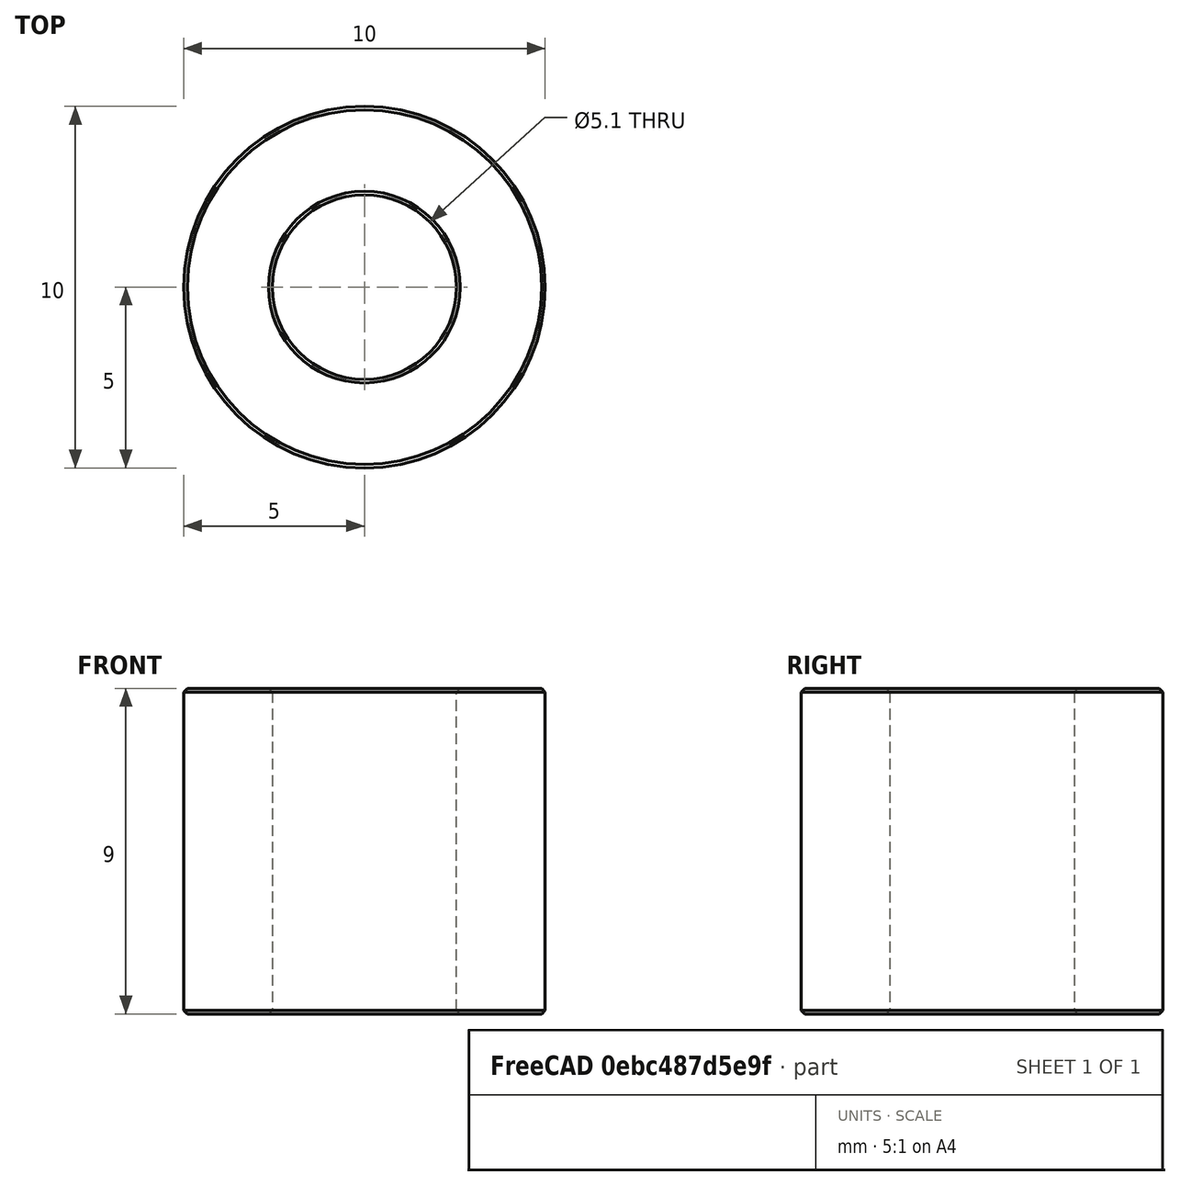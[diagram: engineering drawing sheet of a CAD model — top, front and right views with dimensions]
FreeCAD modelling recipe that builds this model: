
FCSTD DOCUMENT  (FreeCAD 0.20R26683 (Git))
Label: 9mm spacer
License: All rights reserved
LicenseURL: http://en.wikipedia.org/wiki/All_rights_reserved
objects: Sketcher::SketchObject×1, PartDesign::Pad×1, PartDesign::Chamfer×1, PartDesign::Body×1
note: 6 computed .brp shape members not serialized (recipe doc carries the construction recipe); baked Part::Feature solids carry a one-line shape summary decoded from their .brp

FEATURE [Sketcher::SketchObject] Sketch
  FullyConstrained = true
  MapMode = 5
  Support = -> [XY_Plane]
  sketch-geometry (2):
    g0: Circle CenterX=0 CenterY=0 CenterZ=0 NormalX=0 NormalY=0 NormalZ=1 AngleXU=0 Radius=2.55
    g1: Circle CenterX=0 CenterY=0 CenterZ=0 NormalX=0 NormalY=0 NormalZ=1 AngleXU=0 Radius=5
  constraints (4):
    c: Coincident(g0,g-1)
    c: Coincident(g1,g0)
    c: Diameter(g0) = 5.1
    c: Diameter(g1) = 10
FEATURE [PartDesign::Pad] Pad
  Direction = (0,0,1)
  Length = 9
  Length2 = 100
  Profile = -> Sketch
  ReferenceAxis = -> Sketch [N_Axis]
  Refine = true
  Type = 0
FEATURE [PartDesign::Chamfer] Chamfer
  Angle = 45
  Base = -> Pad [Edge6,Edge3,Edge5,Edge2]
  BaseFeature = -> Pad
  ChamferType = 0
  FlipDirection = false
  Refine = true
  Size = 0.1
  Size2 = 1
  SupportTransform = false
FEATURE [PartDesign::Body] Body
  Group = -> [Sketch,Pad,Chamfer]
  Origin = -> Origin
  Tip = -> Chamfer
